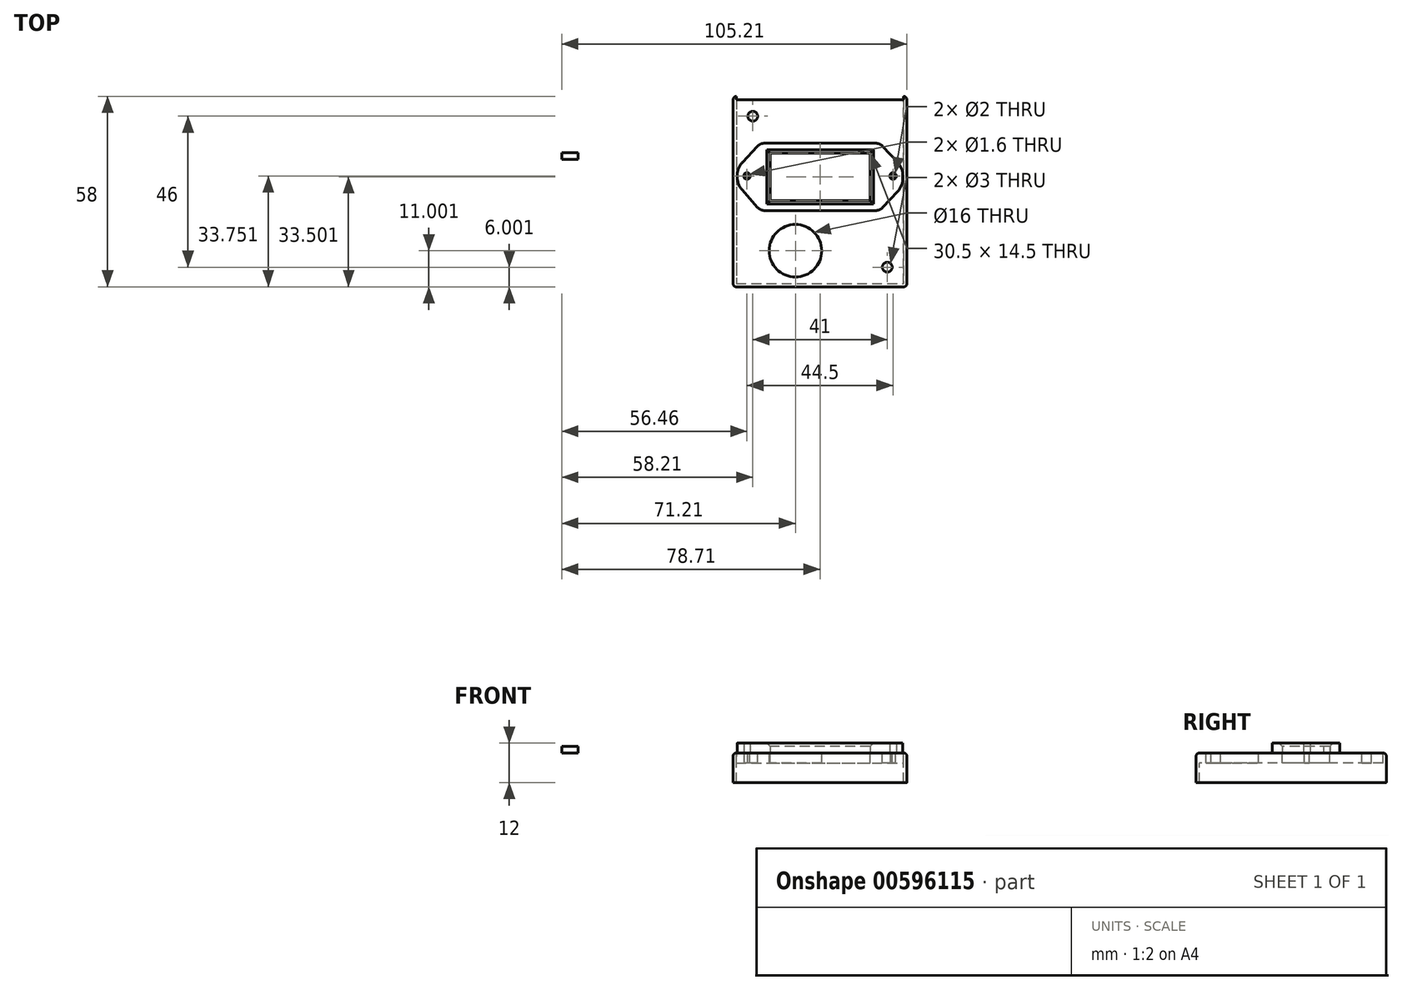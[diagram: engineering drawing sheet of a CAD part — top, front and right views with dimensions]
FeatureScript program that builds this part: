
annotation { "Feature Type Name" : "Feature", "Feature Type Description" : "" }
export const myFeature = defineFeature(function(context is Context, id is Id, definition is map)
    precondition{}
    {
        {
            var Q0;
            Q0=qCreatedBy(makeId("Top.planeOp"),FACE);
            var sketch = newSketch(context, id + "F0", { "sketchPlane" : qUnion([Q0])});
            skLineSegment(sketch, "E0.bottom", {"start": v(25.5, 28) * mm, "end": v(-25.5, 28) * mm});
            skLineSegment(sketch, "E0.top", {"start": v(25.5, -28) * mm, "end": v(-25.5, -28) * mm});
            skLineSegment(sketch, "E0.left", {"start": v(25.5, 28) * mm, "end": v(25.5, -28) * mm});
            skLineSegment(sketch, "E0.right", {"start": v(-25.5, 28) * mm, "end": v(-25.5, -28) * mm});
            skCircle(sketch, "E1", {"center": v(-20.5, 23) * mm, "radius": 1.5 * mm});
            skCircle(sketch, "E2", {"center": v(20.5, -23) * mm, "radius": 1.5 * mm});
            skCircle(sketch, "E3", {"center": v(-7.5, -18) * mm, "radius": 6.1 * mm});
            skLineSegment(sketch, "E4.bottom", {"start": v(-15.25, 11.75) * mm, "end": v(15.25, 11.75) * mm});
            skLineSegment(sketch, "E4.top", {"start": v(-15.25, -2.75) * mm, "end": v(15.25, -2.75) * mm});
            skLineSegment(sketch, "E4.left", {"start": v(-15.25, 11.75) * mm, "end": v(-15.25, -2.75) * mm});
            skLineSegment(sketch, "E4.right", {"start": v(15.25, 11.75) * mm, "end": v(15.25, -2.75) * mm});
            skLineSegment(sketch, "E5.bottom", {"start": v(-2.5, 11.75) * mm, "end": v(2.5, 11.75) * mm});
            skLineSegment(sketch, "E5.top", {"start": v(-2.5, -2.75) * mm, "end": v(2.5, -2.75) * mm});
            skLineSegment(sketch, "E5.left", {"start": v(-2.5, 11.75) * mm, "end": v(-2.5, -2.75) * mm});
            skLineSegment(sketch, "E5.right", {"start": v(2.5, 11.75) * mm, "end": v(2.5, -2.75) * mm});
            skLineSegment(sketch, "E6.bottom", {"start": v(-6.25, 10.5) * mm, "end": v(5.75, 10.5) * mm, "construction": true});
            skLineSegment(sketch, "E6.top", {"start": v(-6.25, -1.5) * mm, "end": v(5.75, -1.5) * mm, "construction": true});
            skLineSegment(sketch, "E6.left", {"start": v(-6.25, 10.5) * mm, "end": v(-6.25, -1.5) * mm, "construction": true});
            skLineSegment(sketch, "E6.right", {"start": v(5.75, 10.5) * mm, "end": v(5.75, -1.5) * mm, "construction": true});
            skLineSegment(sketch, "E7.bottom", {"start": v(-14, 10.5) * mm, "end": v(14, 10.5) * mm, "construction": true});
            skLineSegment(sketch, "E7.top", {"start": v(-14, -1.5) * mm, "end": v(14, -1.5) * mm, "construction": true});
            skLineSegment(sketch, "E7.left", {"start": v(-14, 10.5) * mm, "end": v(-14, -1.5) * mm, "construction": true});
            skLineSegment(sketch, "E7.right", {"start": v(14, 10.5) * mm, "end": v(14, -1.5) * mm, "construction": true});
            skSolve(sketch);
        }
        {
            var Q0;
            Q0=makeQuery(id+"F0.imprint","IMPRINT",FACE,{"disambiguationData":[TD([[makeQuery(id+"F0.imprint","IMPRINT",EDGE,{"derivedFrom":sQuery(id+"F0.wireOp",EDGE,"E0.bottom")}),1.0]])]});
            var Q1;
            Q1=makeQuery(id+"F0.imprint","IMPRINT",FACE,{"disambiguationData":[TD([[makeQuery(id+"F0.imprint","IMPRINT",EDGE,{"derivedFrom":sQuery(id+"F0.wireOp",EDGE,"LN2d2Qam-zQ4N-hJWI-jsZm-hQ2YjQqxJFMe.bottom")}),-1.0]])]});
            var Q2;
            Q2=makeQuery(id+"F0.imprint","IMPRINT",FACE,{"disambiguationData":[TD([[makeQuery(id+"F0.imprint","IMPRINT",EDGE,{"derivedFrom":sQuery(id+"F0.wireOp",EDGE,"Tyq8l7xN-NJ6r-rAiC-5Q4v-MCzvgNdMf9WX.bottom")}),-1.0]])]});
            var Q3;
            Q3=makeQuery(id+"F0.imprint","IMPRINT",FACE,{"disambiguationData":[TD([[makeQuery(id+"F0.imprint","IMPRINT",EDGE,{"derivedFrom":sQuery(id+"F0.wireOp",EDGE,"E5.bottom")}),-1.0]])]});
            var Q4;
            {var subQ12=sQuery(id+"F0.wireOp",EDGE,"5e66b00e-83e9-4da4-8626-02964c2a5a3e.left");Q4=makeQuery(id+"F0.imprint","IMPRINT",FACE,{"disambiguationData":[TD([[makeQuery(id+"F0.imprint","IMPRINT",EDGE,{"derivedFrom":subQ12}),-1.0]])]});}
            var Q5;
            Q5=makeQuery(id+"F0.imprint","IMPRINT",FACE,{"disambiguationData":[TD([[makeQuery(id+"F0.imprint","IMPRINT",EDGE,{"derivedFrom":sQuery(id+"F0.wireOp",EDGE,"242b43d6-e01b-45f4-8fda-c560a832d6e8.bottom")}),-1.0]])]});
            var Q6;
            Q6=makeQuery(id+"F0.imprint","IMPRINT",FACE,{"disambiguationData":[TD([[makeQuery(id+"F0.imprint","IMPRINT",EDGE,{"derivedFrom":sQuery(id+"F0.wireOp",EDGE,"c80b9b78-23ee-44ab-b0c4-abc6401d7a6b.bottom")}),-1.0]])]});
            var Q7;
            Q7=makeQuery(id+"F0.imprint","IMPRINT",FACE,{"disambiguationData":[TD([[makeQuery(id+"F0.imprint","IMPRINT",EDGE,{"derivedFrom":sQuery(id+"F0.wireOp",EDGE,"V3zyF6Pa-9TGi-MSfi-dUwD-Oto6uP0OLka4.bottom")}),-1.0]])]});
            extrude(context, id + "F1", {"entities" : qUnion([Q0, Q1, Q2, Q3, Q4, Q5, Q6, Q7]), "depth" : 1 * mm});
        }
        {
            var Q0;
            Q0=qCreatedBy(makeId("Top.planeOp"),FACE);
            var sketch = newSketch(context, id + "F2", { "sketchPlane" : qUnion([Q0])});
            skPoint(sketch, "E8.middle", {"position": v(28.78, -122.02) * mm});
            skLineSegment(sketch, "E9.bottom", {"start": v(14.21, -108.47) * mm, "end": v(42.21, -108.47) * mm, "construction": true});
            skLineSegment(sketch, "E9.top", {"start": v(14.21, -120.47) * mm, "end": v(42.21, -120.47) * mm, "construction": true});
            skLineSegment(sketch, "E9.left", {"start": v(14.21, -108.47) * mm, "end": v(14.21, -120.47) * mm, "construction": true});
            skLineSegment(sketch, "E9.right", {"start": v(42.21, -108.47) * mm, "end": v(42.21, -120.47) * mm, "construction": true});
            skLineSegment(sketch, "E10.bottom", {"start": v(20.96, -108.47) * mm, "end": v(23.46, -108.47) * mm, "construction": true});
            skLineSegment(sketch, "E10.top", {"start": v(20.96, -120.47) * mm, "end": v(23.46, -120.47) * mm, "construction": true});
            skLineSegment(sketch, "E10.left", {"start": v(20.96, -108.47) * mm, "end": v(20.96, -120.47) * mm, "construction": true});
            skLineSegment(sketch, "E10.right", {"start": v(23.46, -108.47) * mm, "end": v(23.46, -120.47) * mm, "construction": true});
            skLineSegment(sketch, "E11.bottom", {"start": v(32.96, -108.47) * mm, "end": v(35.46, -108.47) * mm, "construction": true});
            skLineSegment(sketch, "E11.top", {"start": v(32.96, -120.47) * mm, "end": v(35.46, -120.47) * mm, "construction": true});
            skLineSegment(sketch, "E11.left", {"start": v(32.96, -108.47) * mm, "end": v(32.96, -120.47) * mm, "construction": true});
            skLineSegment(sketch, "E11.right", {"start": v(35.46, -108.47) * mm, "end": v(35.46, -120.47) * mm, "construction": true});
            skLineSegment(sketch, "E12.bottom", {"start": v(19.21, -111.47) * mm, "end": v(25.21, -111.47) * mm, "construction": true});
            skLineSegment(sketch, "E12.top", {"start": v(19.21, -117.47) * mm, "end": v(25.21, -117.47) * mm, "construction": true});
            skLineSegment(sketch, "E12.left", {"start": v(19.21, -111.47) * mm, "end": v(19.21, -117.47) * mm, "construction": true});
            skLineSegment(sketch, "E12.right", {"start": v(25.21, -111.47) * mm, "end": v(25.21, -117.47) * mm, "construction": true});
            skLineSegment(sketch, "E13.bottom", {"start": v(31.21, -111.47) * mm, "end": v(37.21, -111.47) * mm, "construction": true});
            skLineSegment(sketch, "E13.top", {"start": v(31.21, -117.47) * mm, "end": v(37.21, -117.47) * mm, "construction": true});
            skLineSegment(sketch, "E13.left", {"start": v(31.21, -111.47) * mm, "end": v(31.21, -117.47) * mm, "construction": true});
            skLineSegment(sketch, "E13.right", {"start": v(37.21, -111.47) * mm, "end": v(37.21, -117.47) * mm, "construction": true});
            skLineSegment(sketch, "E14.bottom", {"start": v(2.71, -90.97) * mm, "end": v(53.71, -90.97) * mm});
            skLineSegment(sketch, "E14.top", {"start": v(2.71, -146.97) * mm, "end": v(53.71, -146.97) * mm});
            skLineSegment(sketch, "E14.left", {"start": v(2.71, -90.97) * mm, "end": v(2.71, -146.97) * mm});
            skLineSegment(sketch, "E14.right", {"start": v(53.71, -90.97) * mm, "end": v(53.71, -146.97) * mm});
            skCircle(sketch, "E15", {"center": v(7.71, -95.97) * mm, "radius": 1.5 * mm});
            skCircle(sketch, "E16", {"center": v(48.71, -141.97) * mm, "radius": 1.5 * mm});
            skCircle(sketch, "E17", {"center": v(20.71, -136.97) * mm, "radius": 8 * mm});
            skLineSegment(sketch, "E18.bottom", {"start": v(12.96, -107.22) * mm, "end": v(43.46, -107.22) * mm});
            skLineSegment(sketch, "E18.top", {"start": v(12.96, -121.72) * mm, "end": v(43.46, -121.72) * mm});
            skLineSegment(sketch, "E18.left", {"start": v(12.96, -107.22) * mm, "end": v(12.96, -121.72) * mm});
            skLineSegment(sketch, "E18.right", {"start": v(43.46, -107.22) * mm, "end": v(43.46, -121.72) * mm});
            skPoint(sketch, "E19.middle", {"position": v(-49.22, -118.43) * mm});
            skLineSegment(sketch, "E20.bottom", {"start": v(-62, -102.08) * mm, "end": v(-34, -102.08) * mm});
            skLineSegment(sketch, "E20.top", {"start": v(-62, -114.08) * mm, "end": v(-34, -114.08) * mm});
            skLineSegment(sketch, "E20.left", {"start": v(-62, -102.08) * mm, "end": v(-62, -114.08) * mm});
            skLineSegment(sketch, "E20.right", {"start": v(-34, -102.08) * mm, "end": v(-34, -114.08) * mm});
            skLineSegment(sketch, "E21.bottom", {"start": v(-54.75, -102.08) * mm, "end": v(-52.25, -102.08) * mm, "construction": true});
            skLineSegment(sketch, "E21.top", {"start": v(-54.75, -114.08) * mm, "end": v(-52.25, -114.08) * mm, "construction": true});
            skLineSegment(sketch, "E21.left", {"start": v(-54.75, -102.08) * mm, "end": v(-54.75, -114.08) * mm, "construction": true});
            skLineSegment(sketch, "E21.right", {"start": v(-52.25, -102.08) * mm, "end": v(-52.25, -114.08) * mm, "construction": true});
            skLineSegment(sketch, "E22.bottom", {"start": v(-43.75, -102.08) * mm, "end": v(-41.25, -102.08) * mm, "construction": true});
            skLineSegment(sketch, "E22.top", {"start": v(-43.75, -114.08) * mm, "end": v(-41.25, -114.08) * mm, "construction": true});
            skLineSegment(sketch, "E22.left", {"start": v(-43.75, -102.08) * mm, "end": v(-43.75, -114.08) * mm, "construction": true});
            skLineSegment(sketch, "E22.right", {"start": v(-41.25, -102.08) * mm, "end": v(-41.25, -114.08) * mm, "construction": true});
            skLineSegment(sketch, "E23.bottom", {"start": v(-56.5, -105.08) * mm, "end": v(-50.5, -105.08) * mm, "construction": true});
            skLineSegment(sketch, "E23.top", {"start": v(-56.5, -111.08) * mm, "end": v(-50.5, -111.08) * mm, "construction": true});
            skLineSegment(sketch, "E23.left", {"start": v(-56.5, -105.08) * mm, "end": v(-56.5, -111.08) * mm, "construction": true});
            skLineSegment(sketch, "E23.right", {"start": v(-50.5, -105.08) * mm, "end": v(-50.5, -111.08) * mm, "construction": true});
            skLineSegment(sketch, "E24.bottom", {"start": v(-45.5, -105.08) * mm, "end": v(-39.5, -105.08) * mm, "construction": true});
            skLineSegment(sketch, "E24.top", {"start": v(-45.5, -111.08) * mm, "end": v(-39.5, -111.08) * mm, "construction": true});
            skLineSegment(sketch, "E24.left", {"start": v(-45.5, -105.08) * mm, "end": v(-45.5, -111.08) * mm, "construction": true});
            skLineSegment(sketch, "E24.right", {"start": v(-39.5, -105.08) * mm, "end": v(-39.5, -111.08) * mm, "construction": true});
            skLineSegment(sketch, "E25.bottom", {"start": v(-63, -101.08) * mm, "end": v(-33, -101.08) * mm});
            skLineSegment(sketch, "E25.top", {"start": v(-63, -115.08) * mm, "end": v(-33, -115.08) * mm});
            skLineSegment(sketch, "E25.left", {"start": v(-63, -101.08) * mm, "end": v(-63, -115.08) * mm});
            skLineSegment(sketch, "E25.right", {"start": v(-33, -101.08) * mm, "end": v(-33, -115.08) * mm});
            skLineSegment(sketch, "E26.bottom", {"start": v(-50.5, -107.08) * mm, "end": v(-45.5, -107.08) * mm});
            skLineSegment(sketch, "E26.right", {"start": v(-34, -107.08) * mm, "end": v(-34, -109.08) * mm});
            skLineSegment(sketch, "E27.bottom", {"start": v(-50.5, -102.08) * mm, "end": v(-45.5, -102.08) * mm});
            skLineSegment(sketch, "E27.top", {"start": v(-50.5, -114.08) * mm, "end": v(-45.5, -114.08) * mm});
            skLineSegment(sketch, "E27.left", {"start": v(-50.5, -102.08) * mm, "end": v(-50.5, -114.08) * mm});
            skLineSegment(sketch, "E27.right", {"start": v(-45.5, -102.08) * mm, "end": v(-45.5, -114.08) * mm});
            skLineSegment(sketch, "E28.top", {"start": v(2.71, -89.97) * mm, "end": v(53.71, -89.97) * mm});
            skLineSegment(sketch, "E28.left", {"start": v(2.71, -90.97) * mm, "end": v(2.71, -89.97) * mm});
            skLineSegment(sketch, "E28.right", {"start": v(53.71, -90.97) * mm, "end": v(53.71, -89.97) * mm});
            skLineSegment(sketch, "E29.top", {"start": v(2.71, -147.97) * mm, "end": v(53.71, -147.97) * mm});
            skLineSegment(sketch, "E29.left", {"start": v(2.71, -146.97) * mm, "end": v(2.71, -147.97) * mm});
            skLineSegment(sketch, "E29.right", {"start": v(53.71, -146.97) * mm, "end": v(53.71, -147.97) * mm});
            skLineSegment(sketch, "E30.bottom", {"start": v(53.71, -89.97) * mm, "end": v(54.71, -89.97) * mm});
            skLineSegment(sketch, "E30.top", {"start": v(53.71, -147.97) * mm, "end": v(54.71, -147.97) * mm});
            skLineSegment(sketch, "E30.left", {"start": v(53.71, -89.97) * mm, "end": v(53.71, -147.97) * mm});
            skLineSegment(sketch, "E30.right", {"start": v(54.71, -89.97) * mm, "end": v(54.71, -147.97) * mm});
            skLineSegment(sketch, "E31.bottom", {"start": v(2.71, -89.97) * mm, "end": v(1.71, -89.97) * mm});
            skLineSegment(sketch, "E31.top", {"start": v(2.71, -147.97) * mm, "end": v(1.71, -147.97) * mm});
            skLineSegment(sketch, "E31.left", {"start": v(2.71, -89.97) * mm, "end": v(2.71, -147.97) * mm});
            skLineSegment(sketch, "E31.right", {"start": v(1.71, -89.97) * mm, "end": v(1.71, -147.97) * mm});
            skCircle(sketch, "E32", {"center": v(5.96, -114.22) * mm, "radius": 0.8 * mm});
            skCircle(sketch, "E33", {"center": v(50.46, -114.22) * mm, "radius": 0.8 * mm});
            skLineSegment(sketch, "E34.trimOffspring", {"start": v(-50.5, -109.08) * mm, "end": v(-45.5, -109.08) * mm});
            skSolve(sketch);
        }
        {
            var Q0;
            Q0=qCreatedBy(makeId("Top.planeOp"),FACE);
            var sketch = newSketch(context, id + "F3", { "sketchPlane" : qUnion([Q0])});
            skLineSegment(sketch, "E35.bottom", {"start": v(-65.94, -73.47) * mm, "end": v(-38.14, -73.47) * mm});
            skLineSegment(sketch, "E35.top", {"start": v(-65.94, -85.27) * mm, "end": v(-38.14, -85.27) * mm});
            skLineSegment(sketch, "E35.left", {"start": v(-65.94, -73.47) * mm, "end": v(-65.94, -85.27) * mm});
            skLineSegment(sketch, "E35.right", {"start": v(-38.14, -73.47) * mm, "end": v(-38.14, -85.27) * mm});
            skSolve(sketch);
        }
        {
            var Q0;
            Q0=makeQuery(id+"F1.opExtrude","CAP_FACE",FACE,{"disambiguationData":[OSD([sQuery(id+"F0.wireOp",EDGE,"E0.bottom"),sQuery(id+"F0.wireOp",EDGE,"E0.top"),sQuery(id+"F0.wireOp",EDGE,"E0.left"),sQuery(id+"F0.wireOp",EDGE,"E0.right"),sQuery(id+"F0.wireOp",EDGE,"E1"),sQuery(id+"F0.wireOp",EDGE,"E2"),sQuery(id+"F0.wireOp",EDGE,"E3"),sQuery(id+"F0.wireOp",EDGE,"E4.bottom"),sQuery(id+"F0.wireOp",EDGE,"E4.top"),sQuery(id+"F0.wireOp",EDGE,"E4.left"),sQuery(id+"F0.wireOp",EDGE,"E4.right"),sQuery(id+"F0.wireOp",EDGE,"E5.left"),sQuery(id+"F0.wireOp",EDGE,"E5.right")])],"isStart":false});
            var sketch = newSketch(context, id + "F4", { "sketchPlane" : qUnion([Q0])});
            skLineSegment(sketch, "E36.bottom", {"start": v(-6.25, 10.25) * mm, "end": v(5.75, 10.25) * mm, "construction": true});
            skLineSegment(sketch, "E36.top", {"start": v(-6.25, -1.75) * mm, "end": v(5.75, -1.75) * mm, "construction": true});
            skLineSegment(sketch, "E36.left", {"start": v(-6.25, 10.25) * mm, "end": v(-6.25, -1.75) * mm, "construction": true});
            skLineSegment(sketch, "E36.right", {"start": v(5.75, 10.25) * mm, "end": v(5.75, -1.75) * mm, "construction": true});
            skSolve(sketch);
        }
        {
            var Q0;
            {var subQ3=sQuery(id+"F2.wireOp",EDGE,"E20.left");Q0=makeQuery(id+"F2.imprint","IMPRINT",FACE,{"disambiguationData":[TD([[makeQuery(id+"F2.imprint","IMPRINT",EDGE,{"derivedFrom":subQ3}),-1.0]])]});}
            extrude(context, id + "F5", {"entities" : qUnion([Q0]), "depth" : 4 * mm});
        }
        {
            var Q0;
            Q0=makeQuery(id+"F2.imprint","IMPRINT",FACE,{"disambiguationData":[TD([[makeQuery(id+"F2.imprint","IMPRINT",EDGE,{"derivedFrom":sQuery(id+"F2.wireOp",EDGE,"E15")}),-1.0]])]});
            extrude(context, id + "F6", {"entities" : qUnion([Q0]), "oppositeDirection" : true, "depth" : 3 * mm});
        }
        {
            var Q0;
            Q0=makeQuery(id+"F2.imprint","IMPRINT",FACE,{"disambiguationData":[TD([[makeQuery(id+"F2.imprint","IMPRINT",EDGE,{"derivedFrom":sQuery(id+"F2.wireOp",EDGE,"E26.bottom")}),-1.0]])]});
            var Q1;
            {var subQ5=sQuery(id+"F2.wireOp",EDGE,"E27.bottom");Q1=makeQuery(id+"F2.imprint","IMPRINT",FACE,{"disambiguationData":[TD([[makeQuery(id+"F2.imprint","IMPRINT",EDGE,{"derivedFrom":subQ5}),-1.0]])]});}
            var Q2;
            {var subQ5=sQuery(id+"F2.wireOp",EDGE,"E27.top");Q2=makeQuery(id+"F2.imprint","IMPRINT",FACE,{"disambiguationData":[TD([[makeQuery(id+"F2.imprint","IMPRINT",EDGE,{"derivedFrom":subQ5}),1.0]])]});}
            extrude(context, id + "F7", {"entities" : qUnion([Q0, Q1, Q2]), "operationType" : NewBodyOperationType.ADD, "depth" : 2 * mm});
        }
        {
            var Q0;
            Q0=makeQuery(id+"F3.imprint","IMPRINT",FACE,{"disambiguationData":[TD([[makeQuery(id+"F3.imprint","IMPRINT",EDGE,{"derivedFrom":sQuery(id+"F3.wireOp",EDGE,"E35.bottom")}),-1.0]])]});
            extrude(context, id + "F8", {"entities" : qUnion([Q0]), "depth" : 1.5 * mm});
        }
        {
            var Q0;
            {var subQ3=sQuery(id+"F2.wireOp",EDGE,"E31.bottom");Q0=makeQuery(id+"F2.imprint","IMPRINT",FACE,{"disambiguationData":[TD([[makeQuery(id+"F2.imprint","IMPRINT",EDGE,{"derivedFrom":subQ3}),1.0]])]});}
            var Q1;
            {var subQ0=sQuery(id+"F2.wireOp",EDGE,"E14.bottom");Q1=makeQuery(id+"F2.imprint","IMPRINT",FACE,{"disambiguationData":[TD([[makeQuery(id+"F2.imprint","IMPRINT",EDGE,{"derivedFrom":subQ0}),1.0]])]});}
            var Q2;
            {var subQ0=sQuery(id+"F2.wireOp",EDGE,"E14.top");Q2=makeQuery(id+"F2.imprint","IMPRINT",FACE,{"disambiguationData":[TD([[makeQuery(id+"F2.imprint","IMPRINT",EDGE,{"derivedFrom":subQ0}),-1.0]])]});}
            var Q3;
            {var subQ3=sQuery(id+"F2.wireOp",EDGE,"E30.bottom");Q3=makeQuery(id+"F2.imprint","IMPRINT",FACE,{"disambiguationData":[TD([[makeQuery(id+"F2.imprint","IMPRINT",EDGE,{"derivedFrom":subQ3}),-1.0]])]});}
            extrude(context, id + "F9", {"entities" : qUnion([Q0, Q1, Q2, Q3]), "operationType" : NewBodyOperationType.ADD, "oppositeDirection" : true, "depth" : 9 * mm});
        }
        {
            var Q0;
            Q0=makeQuery(id+"F2.imprint","IMPRINT",FACE,{"disambiguationData":[TD([[makeQuery(id+"F2.imprint","IMPRINT",EDGE,{"derivedFrom":sQuery(id+"F2.wireOp",EDGE,"E15")}),-1.0]])]});
            var sketch = newSketch(context, id + "F10", { "sketchPlane" : qUnion([Q0])});
            skLineSegment(sketch, "E37.bottom", {"start": v(9.96, -104.22) * mm, "end": v(46.46, -104.22) * mm});
            skLineSegment(sketch, "E37.top", {"start": v(9.96, -124.72) * mm, "end": v(46.46, -124.72) * mm});
            skLineSegment(sketch, "E37.left", {"start": v(9.96, -104.22) * mm, "end": v(9.96, -124.72) * mm});
            skLineSegment(sketch, "E37.right", {"start": v(46.46, -104.22) * mm, "end": v(46.46, -124.72) * mm});
            skLineSegment(sketch, "E38", {"start": v(9.96, -124.72) * mm, "end": v(2.96, -116.72) * mm});
            skLineSegment(sketch, "E39", {"start": v(2.96, -116.72) * mm, "end": v(2.96, -111.72) * mm});
            skLineSegment(sketch, "E40", {"start": v(2.96, -111.72) * mm, "end": v(9.96, -104.22) * mm});
            skCircle(sketch, "E41", {"center": v(5.96, -114.22) * mm, "radius": 1 * mm});
            skLineSegment(sketch, "E42.bottom", {"start": v(12.96, -107.22) * mm, "end": v(43.46, -107.22) * mm});
            skLineSegment(sketch, "E42.top", {"start": v(12.96, -121.72) * mm, "end": v(43.46, -121.72) * mm});
            skLineSegment(sketch, "E42.left", {"start": v(12.96, -107.22) * mm, "end": v(12.96, -121.72) * mm});
            skLineSegment(sketch, "E42.right", {"start": v(43.46, -107.22) * mm, "end": v(43.46, -121.72) * mm});
            skLineSegment(sketch, "E43", {"start": v(46.46, -104.22) * mm, "end": v(53.46, -111.72) * mm});
            skLineSegment(sketch, "E44", {"start": v(53.46, -111.72) * mm, "end": v(53.46, -117.22) * mm});
            skLineSegment(sketch, "E45", {"start": v(53.46, -117.22) * mm, "end": v(46.46, -124.72) * mm});
            skCircle(sketch, "E46", {"center": v(50.46, -114.22) * mm, "radius": 1 * mm});
            skSolve(sketch);
        }
        {
            var Q0;
            Q0=qSketchRegion(id+"F10",true);
            extrude(context, id + "F11", {"entities" : qUnion([Q0]), "depth" : 3 * mm});
        }
        {
            var Q0;
            Q0=makeQuery(id+"F11.opExtrude","SWEPT_EDGE",EDGE,{"disambiguationData":[OSD([sQuery(id+"F10.wireOp",EDGE,"E39"),sQuery(id+"F10.wireOp",EDGE,"E40")])]});
            var Q1;
            Q1=makeQuery(id+"F11.opExtrude","SWEPT_EDGE",EDGE,{"disambiguationData":[OSD([sQuery(id+"F10.wireOp",EDGE,"E38"),sQuery(id+"F10.wireOp",EDGE,"E39")])]});
            var Q2;
            Q2=makeQuery(id+"F11.opExtrude","SWEPT_EDGE",EDGE,{"disambiguationData":[OSD([sQuery(id+"F10.wireOp",EDGE,"E44"),sQuery(id+"F10.wireOp",EDGE,"E45")])]});
            var Q3;
            Q3=makeQuery(id+"F11.opExtrude","SWEPT_EDGE",EDGE,{"disambiguationData":[OSD([sQuery(id+"F10.wireOp",EDGE,"E43"),sQuery(id+"F10.wireOp",EDGE,"E44")])]});
            fillet(context, id + "F12", {"entities" : qUnion([Q0, Q1, Q2, Q3]), "radius" : 6 * mm, "tangentPropagation" : true, "allowEdgeOverflow" : false});
        }
        {
            var Q0;
            Q0=makeQuery(id+"F11.opExtrude","SWEPT_EDGE",EDGE,{"disambiguationData":[OSD([sQuery(id+"F10.wireOp",EDGE,"E37.bottom"),sQuery(id+"F10.wireOp",EDGE,"E37.left"),sQuery(id+"F10.wireOp",EDGE,"E40")])]});
            var Q1;
            Q1=makeQuery(id+"F11.opExtrude","SWEPT_EDGE",EDGE,{"disambiguationData":[OSD([sQuery(id+"F10.wireOp",EDGE,"E37.top"),sQuery(id+"F10.wireOp",EDGE,"E37.left"),sQuery(id+"F10.wireOp",EDGE,"E38")])]});
            var Q2;
            Q2=makeQuery(id+"F11.opExtrude","SWEPT_EDGE",EDGE,{"disambiguationData":[OSD([sQuery(id+"F10.wireOp",EDGE,"E37.top"),sQuery(id+"F10.wireOp",EDGE,"E37.right"),sQuery(id+"F10.wireOp",EDGE,"E45")])]});
            var Q3;
            Q3=makeQuery(id+"F11.opExtrude","SWEPT_EDGE",EDGE,{"disambiguationData":[OSD([sQuery(id+"F10.wireOp",EDGE,"E37.bottom"),sQuery(id+"F10.wireOp",EDGE,"E37.right"),sQuery(id+"F10.wireOp",EDGE,"E43")])]});
            fillet(context, id + "F13", {"entities" : qUnion([Q0, Q1, Q2, Q3]), "radius" : 3 * mm, "tangentPropagation" : true, "allowEdgeOverflow" : false});
        }
        {
            var Q0;
            Q0=makeQuery(id+"F9.opExtrude","CAP_EDGE",EDGE,{"disambiguationData":[OSD([sQuery(id+"F2.wireOp",EDGE,"E31.right")])],"isStart":true});
            var Q1;
            Q1=makeQuery(id+"F9.opExtrude","CAP_EDGE",EDGE,{"disambiguationData":[OSD([sQuery(id+"F2.wireOp",EDGE,"E28.top"),sQuery(id+"F2.wireOp",EDGE,"E30.bottom"),sQuery(id+"F2.wireOp",EDGE,"E31.bottom")])],"isStart":true});
            var Q2;
            Q2=makeQuery(id+"F9.opExtrude","CAP_EDGE",EDGE,{"disambiguationData":[OSD([sQuery(id+"F2.wireOp",EDGE,"E29.top"),sQuery(id+"F2.wireOp",EDGE,"E30.top"),sQuery(id+"F2.wireOp",EDGE,"E31.top")])],"isStart":true});
            var Q3;
            Q3=makeQuery(id+"F9.opExtrude","CAP_EDGE",EDGE,{"disambiguationData":[OSD([sQuery(id+"F2.wireOp",EDGE,"E30.right")])],"isStart":true});
            var Q4;
            Q4=makeQuery(id+"F9.opExtrude","SWEPT_EDGE",EDGE,{"disambiguationData":[OSD([sQuery(id+"F2.wireOp",EDGE,"E30.top"),sQuery(id+"F2.wireOp",EDGE,"E30.right")])]});
            var Q5;
            Q5=makeQuery(id+"F9.opExtrude","SWEPT_EDGE",EDGE,{"disambiguationData":[OSD([sQuery(id+"F2.wireOp",EDGE,"E31.top"),sQuery(id+"F2.wireOp",EDGE,"E31.right")])]});
            var Q6;
            Q6=makeQuery(id+"F9.opExtrude","SWEPT_EDGE",EDGE,{"disambiguationData":[OSD([sQuery(id+"F2.wireOp",EDGE,"E31.bottom"),sQuery(id+"F2.wireOp",EDGE,"E31.right")])]});
            var Q7;
            Q7=makeQuery(id+"F9.opExtrude","SWEPT_EDGE",EDGE,{"disambiguationData":[OSD([sQuery(id+"F2.wireOp",EDGE,"E30.bottom"),sQuery(id+"F2.wireOp",EDGE,"E30.right")])]});
            fillet(context, id + "F14", {"entities" : qUnion([Q0, Q1, Q2, Q3, Q4, Q5, Q6, Q7]), "radius" : 1 * mm, "tangentPropagation" : true, "allowEdgeOverflow" : false});
        }
        {
            var Q0;
            Q0=makeQuery(id+"F11.opExtrude","CAP_EDGE",EDGE,{"disambiguationData":[OSD([sQuery(id+"F10.wireOp",EDGE,"E42.left")])],"isStart":false});
            var Q1;
            Q1=makeQuery(id+"F11.opExtrude","CAP_EDGE",EDGE,{"disambiguationData":[OSD([sQuery(id+"F10.wireOp",EDGE,"E42.bottom")])],"isStart":false});
            var Q2;
            Q2=makeQuery(id+"F11.opExtrude","CAP_EDGE",EDGE,{"disambiguationData":[OSD([sQuery(id+"F10.wireOp",EDGE,"E42.right")])],"isStart":false});
            var Q3;
            Q3=makeQuery(id+"F11.opExtrude","CAP_EDGE",EDGE,{"disambiguationData":[OSD([sQuery(id+"F10.wireOp",EDGE,"E42.top")])],"isStart":false});
            chamfer(context, id + "F15", {"entities" : qUnion([Q0, Q1, Q2, Q3]), "width" : 1 * mm, "tangentPropagation" : true});
        }
        {
            var Q0;
            Q0=makeQuery(id+"F1.opExtrude","CAP_FACE",FACE,{"disambiguationData":[OSD([sQuery(id+"F0.wireOp",EDGE,"E0.bottom"),sQuery(id+"F0.wireOp",EDGE,"E0.top"),sQuery(id+"F0.wireOp",EDGE,"E0.left"),sQuery(id+"F0.wireOp",EDGE,"E0.right"),sQuery(id+"F0.wireOp",EDGE,"E1"),sQuery(id+"F0.wireOp",EDGE,"E2"),sQuery(id+"F0.wireOp",EDGE,"E3"),sQuery(id+"F0.wireOp",EDGE,"E4.bottom"),sQuery(id+"F0.wireOp",EDGE,"E4.top"),sQuery(id+"F0.wireOp",EDGE,"E4.left"),sQuery(id+"F0.wireOp",EDGE,"E4.right"),sQuery(id+"F0.wireOp",EDGE,"E5.left"),sQuery(id+"F0.wireOp",EDGE,"E5.right")])],"isStart":false});
            var sketch = newSketch(context, id + "F16", { "sketchPlane" : qUnion([Q0])});
            skCircle(sketch, "E47", {"center": v(-20.5, 23) * mm, "radius": 1.5 * mm});
            skCircle(sketch, "E48", {"center": v(20.5, -23) * mm, "radius": 1.5 * mm});
            skCircle(sketch, "E49", {"center": v(-7.5, -18) * mm, "radius": 8.5 * mm, "construction": true});
            skLineSegment(sketch, "E50.bottom", {"start": v(-25.5, 28) * mm, "end": v(25.5, 28) * mm});
            skLineSegment(sketch, "E50.top", {"start": v(-25.5, -28) * mm, "end": v(25.5, -28) * mm});
            skLineSegment(sketch, "E50.left", {"start": v(-25.5, 28) * mm, "end": v(-25.5, -28) * mm});
            skLineSegment(sketch, "E50.right", {"start": v(25.5, 28) * mm, "end": v(25.5, -28) * mm});
            skLineSegment(sketch, "E51.bottom", {"start": v(-15.25, 11.75) * mm, "end": v(15.25, 11.75) * mm});
            skLineSegment(sketch, "E51.top", {"start": v(-15.25, -2.75) * mm, "end": v(15.25, -2.75) * mm});
            skLineSegment(sketch, "E51.left", {"start": v(-15.25, 11.75) * mm, "end": v(-15.25, -2.75) * mm});
            skLineSegment(sketch, "E51.right", {"start": v(15.25, 11.75) * mm, "end": v(15.25, -2.75) * mm});
            skCircle(sketch, "E52", {"center": v(-22.25, 4.75) * mm, "radius": 2 * mm, "construction": true});
            skCircle(sketch, "E53", {"center": v(22.25, 4.75) * mm, "radius": 2 * mm, "construction": true});
            skLineSegment(sketch, "E54.bottom", {"start": v(5, -27) * mm, "end": v(-20, -27) * mm});
            skLineSegment(sketch, "E54.top", {"start": v(5, -9) * mm, "end": v(-20, -9) * mm});
            skLineSegment(sketch, "E54.left", {"start": v(5, -27) * mm, "end": v(5, -9) * mm});
            skLineSegment(sketch, "E54.right", {"start": v(-20, -27) * mm, "end": v(-20, -9) * mm});
            skSolve(sketch);
        }
        {
            var Q0;
            Q0=makeQuery(id+"F5.opExtrude","CAP_FACE",FACE,{"disambiguationData":[OSD([sQuery(id+"F2.wireOp",EDGE,"E20.bottom"),sQuery(id+"F2.wireOp",EDGE,"E20.top"),sQuery(id+"F2.wireOp",EDGE,"E20.left"),sQuery(id+"F2.wireOp",EDGE,"E20.right"),sQuery(id+"F2.wireOp",EDGE,"E25.bottom"),sQuery(id+"F2.wireOp",EDGE,"E25.top"),sQuery(id+"F2.wireOp",EDGE,"E25.left"),sQuery(id+"F2.wireOp",EDGE,"E25.right"),sQuery(id+"F2.wireOp",EDGE,"E26.left"),sQuery(id+"F2.wireOp",EDGE,"E26.right"),sQuery(id+"F2.wireOp",EDGE,"E27.bottom"),sQuery(id+"F2.wireOp",EDGE,"E27.top")])],"isStart":false});
            var sketch = newSketch(context, id + "F17", { "sketchPlane" : qUnion([Q0])});
            skLineSegment(sketch, "E55.bottom", {"start": v(-63, -101.08) * mm, "end": v(-50.5, -101.08) * mm});
            skLineSegment(sketch, "E55.top", {"start": v(-63, -102.08) * mm, "end": v(-50.5, -102.08) * mm});
            skLineSegment(sketch, "E55.left", {"start": v(-63, -101.08) * mm, "end": v(-63, -102.08) * mm});
            skLineSegment(sketch, "E55.right", {"start": v(-50.5, -101.08) * mm, "end": v(-50.5, -102.08) * mm});
            skLineSegment(sketch, "E56.bottom", {"start": v(-63, -102.08) * mm, "end": v(-62, -102.08) * mm});
            skLineSegment(sketch, "E56.top", {"start": v(-63, -115.08) * mm, "end": v(-62, -115.08) * mm});
            skLineSegment(sketch, "E56.left", {"start": v(-63, -102.08) * mm, "end": v(-63, -115.08) * mm});
            skLineSegment(sketch, "E56.right", {"start": v(-62, -102.08) * mm, "end": v(-62, -115.08) * mm});
            skLineSegment(sketch, "E57.bottom", {"start": v(-50.5, -114.08) * mm, "end": v(-62, -114.08) * mm});
            skLineSegment(sketch, "E57.top", {"start": v(-50.5, -115.08) * mm, "end": v(-62, -115.08) * mm});
            skLineSegment(sketch, "E57.left", {"start": v(-50.5, -114.08) * mm, "end": v(-50.5, -115.08) * mm});
            skLineSegment(sketch, "E57.right", {"start": v(-62, -114.08) * mm, "end": v(-62, -115.08) * mm});
            skLineSegment(sketch, "E58.bottom", {"start": v(-33, -101.08) * mm, "end": v(-45.5, -101.08) * mm});
            skLineSegment(sketch, "E58.top", {"start": v(-33, -102.08) * mm, "end": v(-45.5, -102.08) * mm});
            skLineSegment(sketch, "E58.left", {"start": v(-33, -101.08) * mm, "end": v(-33, -102.08) * mm});
            skLineSegment(sketch, "E58.right", {"start": v(-45.5, -101.08) * mm, "end": v(-45.5, -102.08) * mm});
            skLineSegment(sketch, "E59.bottom", {"start": v(-33, -102.08) * mm, "end": v(-34, -102.08) * mm});
            skLineSegment(sketch, "E59.top", {"start": v(-33, -115.08) * mm, "end": v(-34, -115.08) * mm});
            skLineSegment(sketch, "E59.left", {"start": v(-33, -102.08) * mm, "end": v(-33, -115.08) * mm});
            skLineSegment(sketch, "E59.right", {"start": v(-34, -102.08) * mm, "end": v(-34, -115.08) * mm});
            skLineSegment(sketch, "E60.bottom", {"start": v(-45.5, -114.08) * mm, "end": v(-34, -114.08) * mm});
            skLineSegment(sketch, "E60.top", {"start": v(-45.5, -115.08) * mm, "end": v(-34, -115.08) * mm});
            skLineSegment(sketch, "E60.left", {"start": v(-45.5, -114.08) * mm, "end": v(-45.5, -115.08) * mm});
            skLineSegment(sketch, "E60.right", {"start": v(-34, -114.08) * mm, "end": v(-34, -115.08) * mm});
            skSolve(sketch);
        }
        {
            var Q0;
            {var subQ0=sQuery(id+"F0.wireOp",EDGE,"E3");Q0=makeQuery(id+"FKRJtqk0ZjomfcX_7.boolean.opBoolean","SPLIT",FACE,{"disambiguationData":[TD([makeQuery(id+"F1.opExtrude","SWEPT_FACE",FACE,{"disambiguationData":[OSD([subQ0])]})])],"derivedFrom":makeQuery(id+"F1.opExtrude","CAP_FACE",FACE,{"disambiguationData":[OSD([sQuery(id+"F0.wireOp",EDGE,"E0.bottom"),sQuery(id+"F0.wireOp",EDGE,"E0.top"),sQuery(id+"F0.wireOp",EDGE,"E0.left"),sQuery(id+"F0.wireOp",EDGE,"E0.right"),sQuery(id+"F0.wireOp",EDGE,"E1"),sQuery(id+"F0.wireOp",EDGE,"E2"),subQ0,sQuery(id+"F0.wireOp",EDGE,"E4.bottom"),sQuery(id+"F0.wireOp",EDGE,"E4.top"),sQuery(id+"F0.wireOp",EDGE,"E4.left"),sQuery(id+"F0.wireOp",EDGE,"E4.right"),sQuery(id+"F0.wireOp",EDGE,"E5.left"),sQuery(id+"F0.wireOp",EDGE,"E5.right")])],"isStart":false})});}
            extrude(context, id + "F18", {"entities" : qUnion([Q0]), "operationType" : NewBodyOperationType.ADD, "depth" : 1 * mm});
        }
        {
            var Q0;
            Q0=sQuery(id+"F16.wireOp",VERTEX,"E52.center");
            var Q1;
            Q1=sQuery(id+"F16.wireOp",VERTEX,"E53.center");
            var Q2;
            Q2=makeQuery(id+"F1.opExtrude","SWEPT_BODY",BODY,{"disambiguationData":[OSD([sQuery(id+"F0.wireOp",EDGE,"E0.bottom"),sQuery(id+"F0.wireOp",EDGE,"E0.top"),sQuery(id+"F0.wireOp",EDGE,"E0.left"),sQuery(id+"F0.wireOp",EDGE,"E0.right"),sQuery(id+"F0.wireOp",EDGE,"E1"),sQuery(id+"F0.wireOp",EDGE,"E2"),sQuery(id+"F0.wireOp",EDGE,"E3"),sQuery(id+"F0.wireOp",EDGE,"E4.bottom"),sQuery(id+"F0.wireOp",EDGE,"E4.top"),sQuery(id+"F0.wireOp",EDGE,"E4.left"),sQuery(id+"F0.wireOp",EDGE,"E4.right"),sQuery(id+"F0.wireOp",EDGE,"E5.left"),sQuery(id+"F0.wireOp",EDGE,"E5.right")])]});
            hole(context, id + "F19", {"style" : HoleStyle.SIMPLE, "endStyle" : HoleEndStyle.THROUGH, "holeDiameter" : 1.4 * mm, "isTappedThrough" : true, "tappedDepth" : 12 * mm, "tapClearance" : 3, "locations" : qUnion([Q0, Q1]), "scope" : qUnion([Q2])});
        }
        {
            var Q0;
            {var subQ0=sQuery(id+"F2.wireOp",EDGE,"E27.top");var subQ1=sQuery(id+"F2.wireOp",EDGE,"E27.bottom");var subQ2=sQuery(id+"F2.wireOp",EDGE,"E26.right");var subQ3=sQuery(id+"F2.wireOp",EDGE,"E26.left");Q0=makeQuery(id+"F7.boolean.opBoolean","MERGE",FACE,{"derivedFrom":[makeQuery(id+"F5.opExtrude","CAP_FACE",FACE,{"disambiguationData":[OSD([sQuery(id+"F2.wireOp",EDGE,"E20.bottom"),sQuery(id+"F2.wireOp",EDGE,"E20.top"),sQuery(id+"F2.wireOp",EDGE,"E20.left"),sQuery(id+"F2.wireOp",EDGE,"E20.right"),sQuery(id+"F2.wireOp",EDGE,"E25.bottom"),sQuery(id+"F2.wireOp",EDGE,"E25.top"),sQuery(id+"F2.wireOp",EDGE,"E25.left"),sQuery(id+"F2.wireOp",EDGE,"E25.right"),subQ3,subQ2,subQ1,subQ0])],"isStart":true}),makeQuery(id+"F7.opExtrude","CAP_FACE",FACE,{"disambiguationData":[OSD([sQuery(id+"F2.wireOp",EDGE,"E26.bottom"),sQuery(id+"F2.wireOp",EDGE,"E26.top"),subQ3,subQ2,subQ1,subQ0,sQuery(id+"F2.wireOp",EDGE,"E27.left"),sQuery(id+"F2.wireOp",EDGE,"E27.right")])],"isStart":true})]});}
            var sketch = newSketch(context, id + "F20", { "sketchPlane" : qUnion([Q0])});
            skLineSegment(sketch, "E61.bottom", {"start": v(-63, 115.08) * mm, "end": v(-33, 115.08) * mm});
            skLineSegment(sketch, "E61.top", {"start": v(-63, 114.08) * mm, "end": v(-33, 114.08) * mm});
            skLineSegment(sketch, "E61.left", {"start": v(-63, 115.08) * mm, "end": v(-63, 114.08) * mm});
            skLineSegment(sketch, "E61.right", {"start": v(-33, 115.08) * mm, "end": v(-33, 114.08) * mm});
            skLineSegment(sketch, "E62.bottom", {"start": v(-63, 114.08) * mm, "end": v(-62, 114.08) * mm});
            skLineSegment(sketch, "E62.top", {"start": v(-63, 101.08) * mm, "end": v(-62, 101.08) * mm});
            skLineSegment(sketch, "E62.left", {"start": v(-63, 114.08) * mm, "end": v(-63, 101.08) * mm});
            skLineSegment(sketch, "E62.right", {"start": v(-62, 114.08) * mm, "end": v(-62, 101.08) * mm});
            skLineSegment(sketch, "E63.bottom", {"start": v(-62, 101.08) * mm, "end": v(-33, 101.08) * mm});
            skLineSegment(sketch, "E63.top", {"start": v(-62, 102.08) * mm, "end": v(-33, 102.08) * mm});
            skLineSegment(sketch, "E63.left", {"start": v(-62, 101.08) * mm, "end": v(-62, 102.08) * mm});
            skLineSegment(sketch, "E63.right", {"start": v(-33, 101.08) * mm, "end": v(-33, 102.08) * mm});
            skLineSegment(sketch, "E64.bottom", {"start": v(-33, 114.08) * mm, "end": v(-34, 114.08) * mm});
            skLineSegment(sketch, "E64.top", {"start": v(-33, 102.08) * mm, "end": v(-34, 102.08) * mm});
            skLineSegment(sketch, "E64.left", {"start": v(-33, 114.08) * mm, "end": v(-33, 102.08) * mm});
            skLineSegment(sketch, "E64.right", {"start": v(-34, 114.08) * mm, "end": v(-34, 102.08) * mm});
            skSolve(sketch);
        }
        {
            var Q0;
            Q0=sQuery(id+"F16.wireOp",VERTEX,"E52.center");
            var Q1;
            Q1=sQuery(id+"F16.wireOp",VERTEX,"E53.center");
            var Q2;
            Q2=makeQuery(id+"F1.opExtrude","SWEPT_BODY",BODY,{"disambiguationData":[OSD([sQuery(id+"F0.wireOp",EDGE,"E0.bottom"),sQuery(id+"F0.wireOp",EDGE,"E0.top"),sQuery(id+"F0.wireOp",EDGE,"E0.left"),sQuery(id+"F0.wireOp",EDGE,"E0.right"),sQuery(id+"F0.wireOp",EDGE,"E1"),sQuery(id+"F0.wireOp",EDGE,"E2"),sQuery(id+"F0.wireOp",EDGE,"E3"),sQuery(id+"F0.wireOp",EDGE,"E4.bottom"),sQuery(id+"F0.wireOp",EDGE,"E4.top"),sQuery(id+"F0.wireOp",EDGE,"E4.left"),sQuery(id+"F0.wireOp",EDGE,"E4.right"),sQuery(id+"F0.wireOp",EDGE,"E5.left"),sQuery(id+"F0.wireOp",EDGE,"E5.right")])]});
            hole(context, id + "F21", {"style" : HoleStyle.SIMPLE, "endStyle" : HoleEndStyle.THROUGH, "oppositeDirection" : true, "holeDiameter" : 1.4 * mm, "isTappedThrough" : true, "tappedDepth" : 12 * mm, "tapClearance" : 3, "locations" : qUnion([Q0, Q1]), "scope" : qUnion([Q2])});
        }
        {
            var Q0;
            Q0=makeQuery(id+"F16.imprint","IMPRINT",FACE,{"disambiguationData":[TD([[makeQuery(id+"F16.imprint","IMPRINT",EDGE,{"derivedFrom":sQuery(id+"F16.wireOp",EDGE,"E47")}),-1.0]])]});
            extrude(context, id + "F22", {"entities" : qUnion([Q0]), "operationType" : NewBodyOperationType.ADD, "depth" : 5 * mm});
        }
        {
            var Q0;
            Q0=makeQuery(id+"F1.opExtrude","CAP_FACE",FACE,{"disambiguationData":[OSD([sQuery(id+"F0.wireOp",EDGE,"E0.bottom"),sQuery(id+"F0.wireOp",EDGE,"E0.top"),sQuery(id+"F0.wireOp",EDGE,"E0.left"),sQuery(id+"F0.wireOp",EDGE,"E0.right"),sQuery(id+"F0.wireOp",EDGE,"E1"),sQuery(id+"F0.wireOp",EDGE,"E2"),sQuery(id+"F0.wireOp",EDGE,"E3"),sQuery(id+"F0.wireOp",EDGE,"E4.bottom"),sQuery(id+"F0.wireOp",EDGE,"E4.top"),sQuery(id+"F0.wireOp",EDGE,"E4.left"),sQuery(id+"F0.wireOp",EDGE,"E4.right"),sQuery(id+"F0.wireOp",EDGE,"E5.left"),sQuery(id+"F0.wireOp",EDGE,"E5.right")])],"isStart":true});
            var sketch = newSketch(context, id + "F23", { "sketchPlane" : qUnion([Q0])});
            skLineSegment(sketch, "E65.bottom", {"start": v(-25.5, 28) * mm, "end": v(25.5, 28) * mm});
            skLineSegment(sketch, "E65.top", {"start": v(-25.5, 27.8) * mm, "end": v(25.5, 27.8) * mm});
            skLineSegment(sketch, "E65.left", {"start": v(-25.5, 28) * mm, "end": v(-25.5, 27.8) * mm});
            skLineSegment(sketch, "E65.right", {"start": v(25.5, 28) * mm, "end": v(25.5, 27.8) * mm});
            skLineSegment(sketch, "E66.bottom", {"start": v(-25.5, -28) * mm, "end": v(25.5, -28) * mm});
            skLineSegment(sketch, "E66.top", {"start": v(-25.5, -27.8) * mm, "end": v(25.5, -27.8) * mm});
            skLineSegment(sketch, "E66.left", {"start": v(-25.5, -28) * mm, "end": v(-25.5, -27.8) * mm});
            skLineSegment(sketch, "E66.right", {"start": v(25.5, -28) * mm, "end": v(25.5, -27.8) * mm});
            skLineSegment(sketch, "E67.bottom", {"start": v(-25.5, -27.8) * mm, "end": v(-25.3, -27.8) * mm});
            skLineSegment(sketch, "E67.top", {"start": v(-25.5, 27.8) * mm, "end": v(-25.3, 27.8) * mm});
            skLineSegment(sketch, "E67.left", {"start": v(-25.5, -27.8) * mm, "end": v(-25.5, 27.8) * mm});
            skLineSegment(sketch, "E67.right", {"start": v(-25.3, -27.8) * mm, "end": v(-25.3, 27.8) * mm});
            skLineSegment(sketch, "E68.bottom", {"start": v(25.5, -27.8) * mm, "end": v(25.3, -27.8) * mm});
            skLineSegment(sketch, "E68.top", {"start": v(25.5, 27.8) * mm, "end": v(25.3, 27.8) * mm});
            skLineSegment(sketch, "E68.left", {"start": v(25.5, -27.8) * mm, "end": v(25.5, 27.8) * mm});
            skLineSegment(sketch, "E68.right", {"start": v(25.3, -27.8) * mm, "end": v(25.3, 27.8) * mm});
            skSolve(sketch);
        }
        {
            var Q0;
            Q0=qSketchRegion(id+"F23",true);
            extrude(context, id + "F24", {"entities" : qUnion([Q0]), "operationType" : NewBodyOperationType.REMOVE, "oppositeDirection" : true, "depth" : 25 * mm});
        }
        {
            var Q0;
            Q0=sQuery(id+"F16.wireOp",VERTEX,"E52.center");
            var Q1;
            Q1=sQuery(id+"F16.wireOp",VERTEX,"E53.center");
            var Q2;
            Q2=makeQuery(id+"F1.opExtrude","SWEPT_BODY",BODY,{"disambiguationData":[OSD([sQuery(id+"F0.wireOp",EDGE,"E0.bottom"),sQuery(id+"F0.wireOp",EDGE,"E0.top"),sQuery(id+"F0.wireOp",EDGE,"E0.left"),sQuery(id+"F0.wireOp",EDGE,"E0.right"),sQuery(id+"F0.wireOp",EDGE,"E1"),sQuery(id+"F0.wireOp",EDGE,"E2"),sQuery(id+"F0.wireOp",EDGE,"E3"),sQuery(id+"F0.wireOp",EDGE,"E4.bottom"),sQuery(id+"F0.wireOp",EDGE,"E4.top"),sQuery(id+"F0.wireOp",EDGE,"E4.left"),sQuery(id+"F0.wireOp",EDGE,"E4.right"),sQuery(id+"F0.wireOp",EDGE,"E5.left"),sQuery(id+"F0.wireOp",EDGE,"E5.right")])]});
            hole(context, id + "F25", {"style" : HoleStyle.SIMPLE, "endStyle" : HoleEndStyle.THROUGH, "oppositeDirection" : true, "holeDiameter" : 1.6 * mm, "isTappedThrough" : true, "tappedDepth" : 12 * mm, "tapClearance" : 3, "locations" : qUnion([Q0, Q1]), "scope" : qUnion([Q2])});
        }
        {
            var Q0;
            Q0=sQuery(id+"F16.wireOp",VERTEX,"E53.center");
            var Q1;
            Q1=sQuery(id+"F16.wireOp",VERTEX,"E52.center");
            var Q2;
            Q2=makeQuery(id+"F1.opExtrude","SWEPT_BODY",BODY,{"disambiguationData":[OSD([sQuery(id+"F0.wireOp",EDGE,"E0.bottom"),sQuery(id+"F0.wireOp",EDGE,"E0.top"),sQuery(id+"F0.wireOp",EDGE,"E0.left"),sQuery(id+"F0.wireOp",EDGE,"E0.right"),sQuery(id+"F0.wireOp",EDGE,"E1"),sQuery(id+"F0.wireOp",EDGE,"E2"),sQuery(id+"F0.wireOp",EDGE,"E3"),sQuery(id+"F0.wireOp",EDGE,"E4.bottom"),sQuery(id+"F0.wireOp",EDGE,"E4.top"),sQuery(id+"F0.wireOp",EDGE,"E4.left"),sQuery(id+"F0.wireOp",EDGE,"E4.right"),sQuery(id+"F0.wireOp",EDGE,"E5.left"),sQuery(id+"F0.wireOp",EDGE,"E5.right")])]});
            hole(context, id + "F26", {"style" : HoleStyle.SIMPLE, "endStyle" : HoleEndStyle.THROUGH, "holeDiameter" : 1.6 * mm, "isTappedThrough" : true, "tappedDepth" : 12 * mm, "tapClearance" : 3, "locations" : qUnion([Q0, Q1]), "scope" : qUnion([Q2])});
        }
        {
            var Q0;
            Q0=makeQuery(id+"F1.opExtrude","SWEPT_BODY",BODY,{"disambiguationData":[OSD([sQuery(id+"F0.wireOp",EDGE,"E0.bottom"),sQuery(id+"F0.wireOp",EDGE,"E0.top"),sQuery(id+"F0.wireOp",EDGE,"E0.left"),sQuery(id+"F0.wireOp",EDGE,"E0.right"),sQuery(id+"F0.wireOp",EDGE,"E1"),sQuery(id+"F0.wireOp",EDGE,"E2"),sQuery(id+"F0.wireOp",EDGE,"E3"),sQuery(id+"F0.wireOp",EDGE,"E4.bottom"),sQuery(id+"F0.wireOp",EDGE,"E4.top"),sQuery(id+"F0.wireOp",EDGE,"E4.left"),sQuery(id+"F0.wireOp",EDGE,"E4.right"),sQuery(id+"F0.wireOp",EDGE,"E5.left"),sQuery(id+"F0.wireOp",EDGE,"E5.right")])]});
            var Q1;
            Q1=makeQuery(id+"F8.opExtrude","SWEPT_BODY",BODY,{"disambiguationData":[OSD([sQuery(id+"F3.wireOp",EDGE,"E35.bottom"),sQuery(id+"F3.wireOp",EDGE,"E35.top"),sQuery(id+"F3.wireOp",EDGE,"E35.left"),sQuery(id+"F3.wireOp",EDGE,"E35.right")])]});
            var Q2;
            Q2=makeQuery(id+"F5.opExtrude","SWEPT_BODY",BODY,{"disambiguationData":[OSD([sQuery(id+"F2.wireOp",EDGE,"E20.bottom"),sQuery(id+"F2.wireOp",EDGE,"E20.top"),sQuery(id+"F2.wireOp",EDGE,"E20.left"),sQuery(id+"F2.wireOp",EDGE,"E20.right"),sQuery(id+"F2.wireOp",EDGE,"E25.bottom"),sQuery(id+"F2.wireOp",EDGE,"E25.top"),sQuery(id+"F2.wireOp",EDGE,"E25.left"),sQuery(id+"F2.wireOp",EDGE,"E25.right"),sQuery(id+"F2.wireOp",EDGE,"E26.right"),sQuery(id+"F2.wireOp",EDGE,"E27.bottom"),sQuery(id+"F2.wireOp",EDGE,"E27.top")])]});
            deleteBodies(context, id + "F27", {"entities" : qUnion([Q0, Q1, Q2])});
        }
    });
